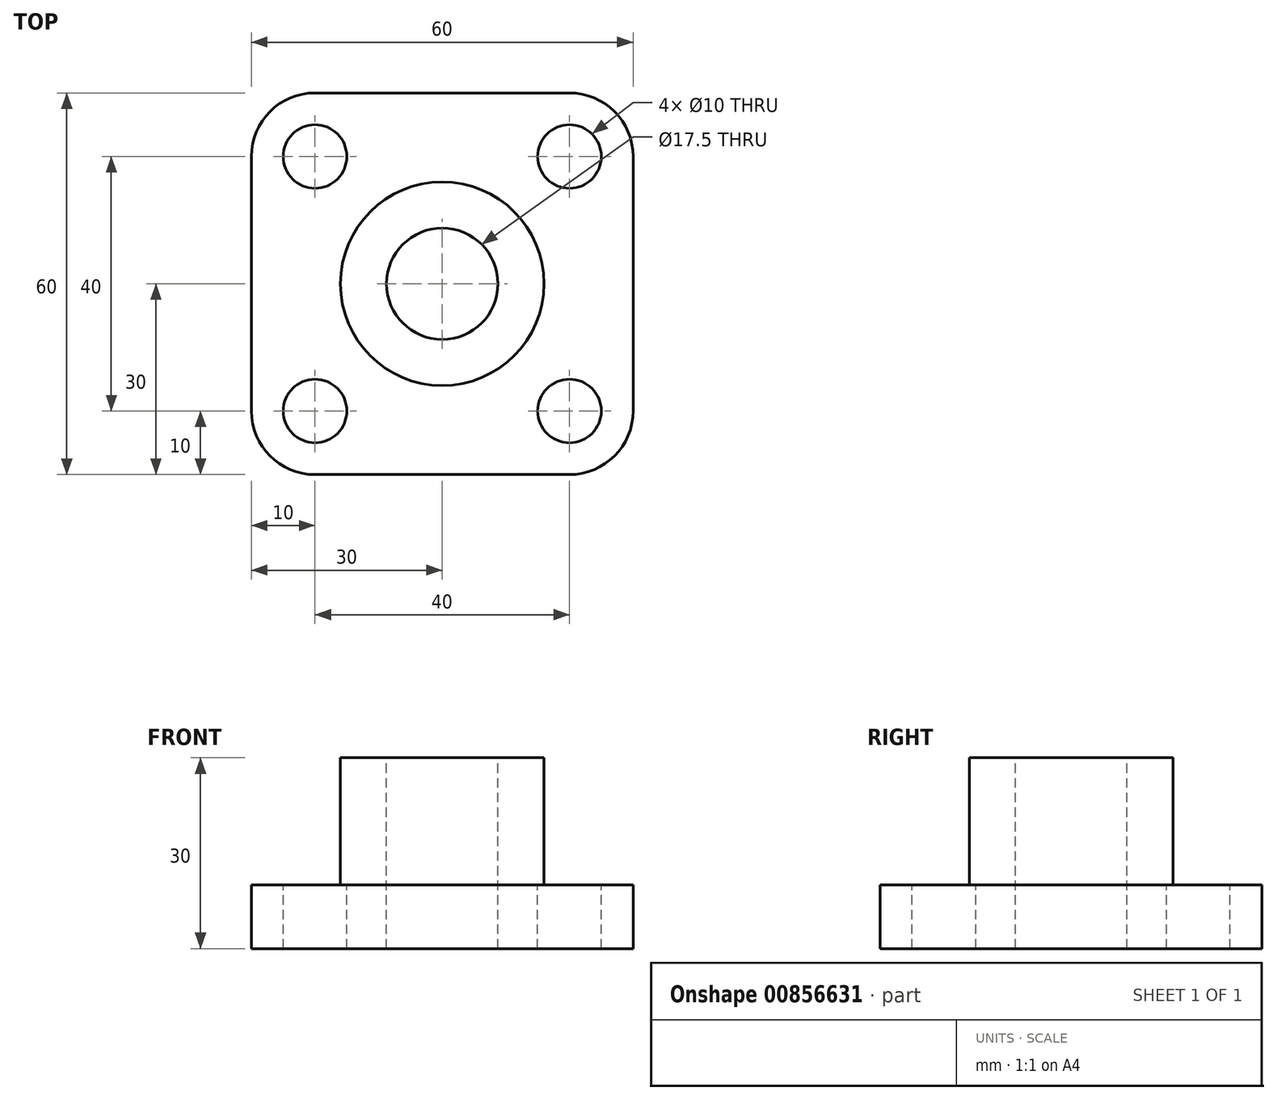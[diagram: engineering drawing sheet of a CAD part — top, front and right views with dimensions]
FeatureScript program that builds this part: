
annotation { "Feature Type Name" : "Feature", "Feature Type Description" : "" }
export const myFeature = defineFeature(function(context is Context, id is Id, definition is map)
    precondition{}
    {
        {
            var Q0;
            Q0=qCreatedBy(makeId("Top.planeOp"),FACE);
            var sketch = newSketch(context, id + "F0", { "sketchPlane" : qUnion([Q0])});
            skLineSegment(sketch, "E0.bottom", {"start": v(30, 30) * mm, "end": v(-30, 30) * mm});
            skLineSegment(sketch, "E0.top", {"start": v(30, -30) * mm, "end": v(-30, -30) * mm});
            skLineSegment(sketch, "E0.left", {"start": v(30, 30) * mm, "end": v(30, -30) * mm});
            skLineSegment(sketch, "E0.right", {"start": v(-30, 30) * mm, "end": v(-30, -30) * mm});
            skPoint(sketch, "E0.middle", {"position": v(0, 0) * mm});
            skSolve(sketch);
        }
        {
            var Q0;
            Q0=makeQuery(id+"F0.imprint","IMPRINT",FACE,{"disambiguationData":[TD([[makeQuery(id+"F0.imprint","IMPRINT",EDGE,{"derivedFrom":sQuery(id+"F0.wireOp",EDGE,"E0.bottom")}),1.0]])]});
            extrude(context, id + "F1", {"entities" : qUnion([Q0]), "depth" : 10 * mm, "offsetDistance" : 25 * mm});
        }
        {
            var Q0;
            Q0=makeQuery(id+"F1.opExtrude","SWEPT_EDGE",EDGE,{"disambiguationData":[OSD([sQuery(id+"F0.wireOp",EDGE,"E0.bottom"),sQuery(id+"F0.wireOp",EDGE,"E0.right")])]});
            var Q1;
            Q1=makeQuery(id+"F1.opExtrude","SWEPT_EDGE",EDGE,{"disambiguationData":[OSD([sQuery(id+"F0.wireOp",EDGE,"E0.top"),sQuery(id+"F0.wireOp",EDGE,"E0.right")])]});
            var Q2;
            Q2=makeQuery(id+"F1.opExtrude","SWEPT_EDGE",EDGE,{"disambiguationData":[OSD([sQuery(id+"F0.wireOp",EDGE,"E0.top"),sQuery(id+"F0.wireOp",EDGE,"E0.left")])]});
            var Q3;
            Q3=makeQuery(id+"F1.opExtrude","SWEPT_EDGE",EDGE,{"disambiguationData":[OSD([sQuery(id+"F0.wireOp",EDGE,"E0.bottom"),sQuery(id+"F0.wireOp",EDGE,"E0.left")])]});
            fillet(context, id + "F2", {"entities" : qUnion([Q0, Q1, Q2, Q3]), "radius" : 10 * mm, "tangentPropagation" : true, "allowEdgeOverflow" : false});
        }
        {
            var Q0;
            Q0=makeQuery(id+"F1.opExtrude","CAP_FACE",FACE,{"disambiguationData":[OSD([sQuery(id+"F0.wireOp",EDGE,"E0.bottom"),sQuery(id+"F0.wireOp",EDGE,"E0.top"),sQuery(id+"F0.wireOp",EDGE,"E0.left"),sQuery(id+"F0.wireOp",EDGE,"E0.right")])],"isStart":false});
            var sketch = newSketch(context, id + "F3", { "sketchPlane" : qUnion([Q0])});
            skLineSegment(sketch, "E1.bottom", {"start": v(20, 20) * mm, "end": v(-20, 20) * mm});
            skLineSegment(sketch, "E1.top", {"start": v(20, -20) * mm, "end": v(-20, -20) * mm});
            skLineSegment(sketch, "E1.left", {"start": v(20, 20) * mm, "end": v(20, -20) * mm});
            skLineSegment(sketch, "E1.right", {"start": v(-20, 20) * mm, "end": v(-20, -20) * mm});
            skPoint(sketch, "E1.middle", {"position": v(0, 0) * mm});
            skPoint(sketch, "E2", {"position": v(-20, 20) * mm});
            skPoint(sketch, "E3", {"position": v(20, 20) * mm});
            skPoint(sketch, "E4", {"position": v(20, -20) * mm});
            skPoint(sketch, "E5", {"position": v(-20, -20) * mm});
            skSolve(sketch);
        }
        {
            var Q0;
            Q0=sQuery(id+"F3.wireOp",VERTEX,"E2");
            var Q1;
            Q1=sQuery(id+"F3.wireOp",VERTEX,"E3");
            var Q2;
            Q2=sQuery(id+"F3.wireOp",VERTEX,"E4");
            var Q3;
            Q3=sQuery(id+"F3.wireOp",VERTEX,"E5");
            var Q4;
            Q4=makeQuery(id+"F1.opExtrude","SWEPT_BODY",BODY,{"disambiguationData":[OSD([sQuery(id+"F0.wireOp",EDGE,"E0.bottom"),sQuery(id+"F0.wireOp",EDGE,"E0.top"),sQuery(id+"F0.wireOp",EDGE,"E0.left"),sQuery(id+"F0.wireOp",EDGE,"E0.right")])]});
            hole(context, id + "F4", {"style" : HoleStyle.SIMPLE, "endStyle" : HoleEndStyle.BLIND, "holeDiameter" : 10 * mm, "majorDiameter" : 5 * mm, "holeDepth" : 10 * mm, "isTappedThrough" : true, "tappedDepth" : 19 * mm, "tapClearance" : 3, "locations" : qUnion([Q0, Q1, Q2, Q3]), "scope" : qUnion([Q4])});
        }
        {
            var Q0;
            Q0=makeQuery(id+"F1.opExtrude","CAP_FACE",FACE,{"disambiguationData":[OSD([sQuery(id+"F0.wireOp",EDGE,"E0.bottom"),sQuery(id+"F0.wireOp",EDGE,"E0.top"),sQuery(id+"F0.wireOp",EDGE,"E0.left"),sQuery(id+"F0.wireOp",EDGE,"E0.right")])],"isStart":false});
            var sketch = newSketch(context, id + "F5", { "sketchPlane" : qUnion([Q0])});
            skCircle(sketch, "E6", {"center": v(0, 0) * mm, "radius": 16 * mm});
            skSolve(sketch);
        }
        {
            var Q0;
            Q0=makeQuery(id+"F5.imprint","IMPRINT",FACE,{"disambiguationData":[TD([[makeQuery(id+"F5.imprint","IMPRINT",EDGE,{"derivedFrom":sQuery(id+"F5.wireOp",EDGE,"E6")}),1.0]])]});
            extrude(context, id + "F6", {"entities" : qUnion([Q0]), "operationType" : NewBodyOperationType.ADD, "depth" : 20 * mm, "offsetDistance" : 25 * mm});
        }
        {
            var Q0;
            Q0=makeQuery(id+"F6.opExtrude","CAP_FACE",FACE,{"disambiguationData":[OSD([sQuery(id+"F5.wireOp",EDGE,"E6")])],"isStart":false});
            var sketch = newSketch(context, id + "F7", { "sketchPlane" : qUnion([Q0])});
            skPoint(sketch, "E7", {"position": v(0, 0) * mm});
            skSolve(sketch);
        }
        {
            var Q0;
            Q0=sQuery(id+"F7.wireOp",VERTEX,"E7");
            var Q1;
            Q1=makeQuery(id+"F1.opExtrude","SWEPT_BODY",BODY,{"disambiguationData":[OSD([sQuery(id+"F0.wireOp",EDGE,"E0.bottom"),sQuery(id+"F0.wireOp",EDGE,"E0.top"),sQuery(id+"F0.wireOp",EDGE,"E0.left"),sQuery(id+"F0.wireOp",EDGE,"E0.right")])]});
            hole(context, id + "F8", {"style" : HoleStyle.SIMPLE, "endStyle" : HoleEndStyle.BLIND, "standardTappedOrClearance" : lookupTablePath({ "fit" : "Normal", "standard" : "ISO", "size" : "M16", "type" : "Clearance" }), "standardBlindInLast" : lookupTablePath({ "fit" : "Standard", "standard" : "ISO", "size" : "M16", "type" : "Clearance" }), "holeDiameter" : 17.5 * mm, "majorDiameter" : 5 * mm, "holeDepth" : 30 * mm, "isTappedThrough" : true, "tappedDepth" : 19 * mm, "tapClearance" : 3, "locations" : qUnion([Q0]), "scope" : qUnion([Q1])});
        }
    });
